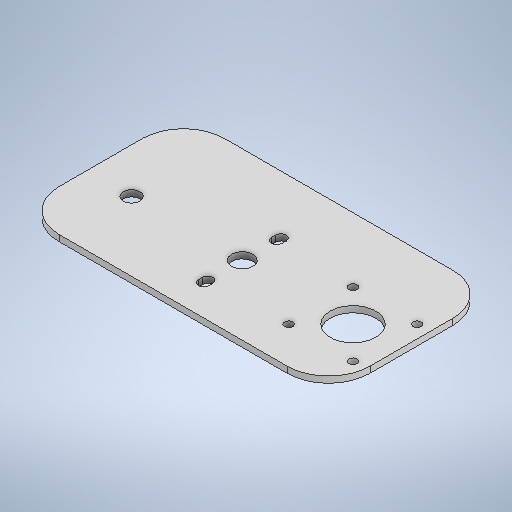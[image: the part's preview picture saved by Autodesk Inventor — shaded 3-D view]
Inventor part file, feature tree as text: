
AUTODESK INVENTOR PART (.ipt)
format: ipt  version: 2025.2 (Build 292293000, 293)  size: 290,816 bytes
history: native  units: mm
features: extrude x3, sketch x3, fillet x1
ambient origin geometry x8: Origin, YZ Plane, XZ Plane, XY Plane, X Axis, Y Axis, Z Axis, Center Point
bodies: Solid1 (feature_tree)
feature tree (7):
  extrude  "Extrusion1"  Depth=80.0mm
  extrude  "Extrusion4"  Depth=3.0mm
  extrude  "Extrusion6"  Depth=150.0mm
  fillet  "Fillet1"  Radius=43.2mm
  sketch  "Sketch1"  dims[d0=150.0mm d1=80.0mm]
  sketch  "Sketch5"  dims[d2=3.0mm d3=0.0mm d26=25.0mm]
  sketch  "Sketch6"  dims[d36=0.0mm d37=0.0mm d49=150.0mm d50=43.2mm d51=43.2mm d52=22.0mm d53=31.0mm d54=31.0mm d55=4.0mm d56=4.0mm d57=4.0mm d58=4.0mm d59=25.0mm d60=43.2mm d61=43.2mm d62=43.2mm d63=10.2mm d64=43.2mm d65=53.4mm d66=8.0mm d67=0.0mm d68=0.0mm d69=37.3mm d70=5.0mm d71=2.0mm d72=5.0mm d73=5.0mm d74=2.0mm d75=5.0mm d87=20.0mm d27=0.872665mm d28=0.5mm d29=0.872665mm]
